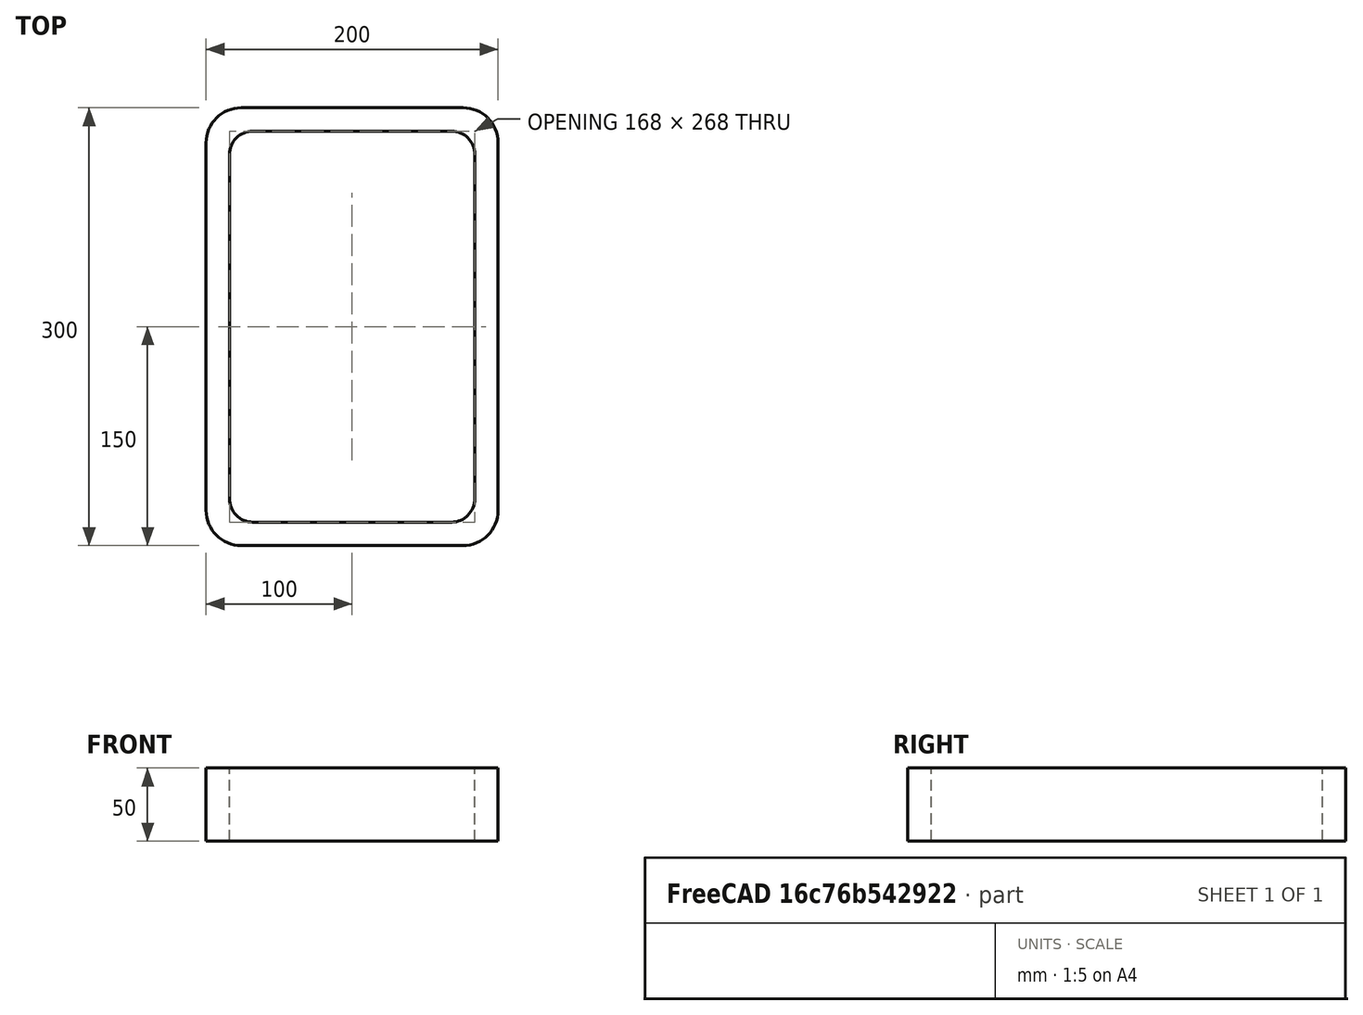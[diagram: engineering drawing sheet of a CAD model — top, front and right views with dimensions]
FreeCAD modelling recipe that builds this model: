
FCSTD DOCUMENT  (FreeCAD 0.15R4671 (Git))
Label: Rectangular hollow section 300x200x16 EN10219 S235JRH
License: All rights reserved
LicenseURL: http://en.wikipedia.org/wiki/All_rights_reserved
objects: Sketcher::SketchObject×1, Part::Extrusion×1
note: 2 computed .brp shape members not serialized (recipe doc carries the construction recipe); baked Part::Feature solids carry a one-line shape summary decoded from their .brp

FEATURE [Sketcher::SketchObject] Sketch
  sketch-geometry (16):
    g0: LineSegment StartX=-68 StartY=134 StartZ=0 EndX=68 EndY=134 EndZ=0
    g1: LineSegment StartX=84 StartY=118 StartZ=0 EndX=84 EndY=-118 EndZ=0
    g2: LineSegment StartX=68 StartY=-134 StartZ=0 EndX=-68 EndY=-134 EndZ=0
    g3: LineSegment StartX=-84 StartY=-118 StartZ=0 EndX=-84 EndY=118 EndZ=0
    g4: LineSegment StartX=-76 StartY=150 StartZ=0 EndX=76 EndY=150 EndZ=0
    g5: LineSegment StartX=100 StartY=126 StartZ=0 EndX=100 EndY=-126 EndZ=0
    g6: LineSegment StartX=76 StartY=-150 StartZ=0 EndX=-76 EndY=-150 EndZ=0
    g7: LineSegment StartX=-100 StartY=-126 StartZ=0 EndX=-100 EndY=126 EndZ=0
    g8: ArcOfCircle CenterX=-68 CenterY=118 CenterZ=0 NormalX=0 NormalY=0 NormalZ=1 Radius=16 StartAngle=1.5708 EndAngle=3.14159
    g9: ArcOfCircle CenterX=68 CenterY=118 CenterZ=0 NormalX=0 NormalY=0 NormalZ=1 Radius=16 StartAngle=0 EndAngle=1.5708
    g10: ArcOfCircle CenterX=68 CenterY=-118 CenterZ=0 NormalX=0 NormalY=0 NormalZ=1 Radius=16 StartAngle=4.71239 EndAngle=6.28319
    g11: ArcOfCircle CenterX=-68 CenterY=-118 CenterZ=0 NormalX=0 NormalY=0 NormalZ=1 Radius=16 StartAngle=3.14159 EndAngle=4.71239
    g12: ArcOfCircle CenterX=76 CenterY=126 CenterZ=0 NormalX=0 NormalY=0 NormalZ=1 Radius=24 StartAngle=0 EndAngle=1.5708
    g13: ArcOfCircle CenterX=76 CenterY=-126 CenterZ=0 NormalX=0 NormalY=0 NormalZ=1 Radius=24 StartAngle=4.71239 EndAngle=6.28319
    g14: ArcOfCircle CenterX=-76 CenterY=-126 CenterZ=0 NormalX=0 NormalY=0 NormalZ=1 Radius=24 StartAngle=3.14159 EndAngle=4.71239
    g15: ArcOfCircle CenterX=-76 CenterY=126 CenterZ=0 NormalX=0 NormalY=0 NormalZ=1 Radius=24 StartAngle=1.5708 EndAngle=3.14159
  constraints (36):
    c: Horizontal(g2)
    c: Vertical(g3)
    c: Horizontal(g6)
    c: Vertical(g7)
    c: Tangent(g3,g8) = 1.5708
    c: Tangent(g0,g8) = 1.5708
    c: Tangent(g0,g9) = 1.5708
    c: Tangent(g1,g9) = 1.5708
    c: Tangent(g1,g10) = 1.5708
    c: Tangent(g2,g10) = 1.5708
    c: Tangent(g2,g11) = 1.5708
    c: Tangent(g3,g11) = 1.5708
    c: Tangent(g4,g12) = 1.5708
    c: Tangent(g5,g12) = 1.5708
    c: Tangent(g5,g13) = 1.5708
    c: Tangent(g6,g13) = 1.5708
    c: Tangent(g6,g14) = 1.5708
    c: Tangent(g7,g14) = 1.5708
    c: Tangent(g7,g15) = 1.5708
    c: Tangent(g4,g15) = 1.5708
    c: Equal(g9,g8)
    c: Equal(g9,g11)
    c: Equal(g9,g10)
    c: Equal(g12,g15)
    c: Equal(g12,g14)
    c: Equal(g12,g13)
    c: Symmetric(g4,g6,g-1)
    c: Symmetric(g7,g5,g-2)
    c: DistanceY(g4,g6) = -300
    c: DistanceX(g7,g5) = 200
    c: Symmetric(g3,g1,g-2)
    c: Symmetric(g0,g2,g-1)
    c: DistanceY(g0,g4) = 16
    c: DistanceX(g5,g1) = -16
    c: Radius(g9) = 16
    c: Radius(g12) = 24
FEATURE [Part::Extrusion] Extrude  label="Rectangular hollow section 300x200x16 EN10219 S235JRH"
  Base = -> Sketch
  Dir = (0,0,50)
  Solid = true
